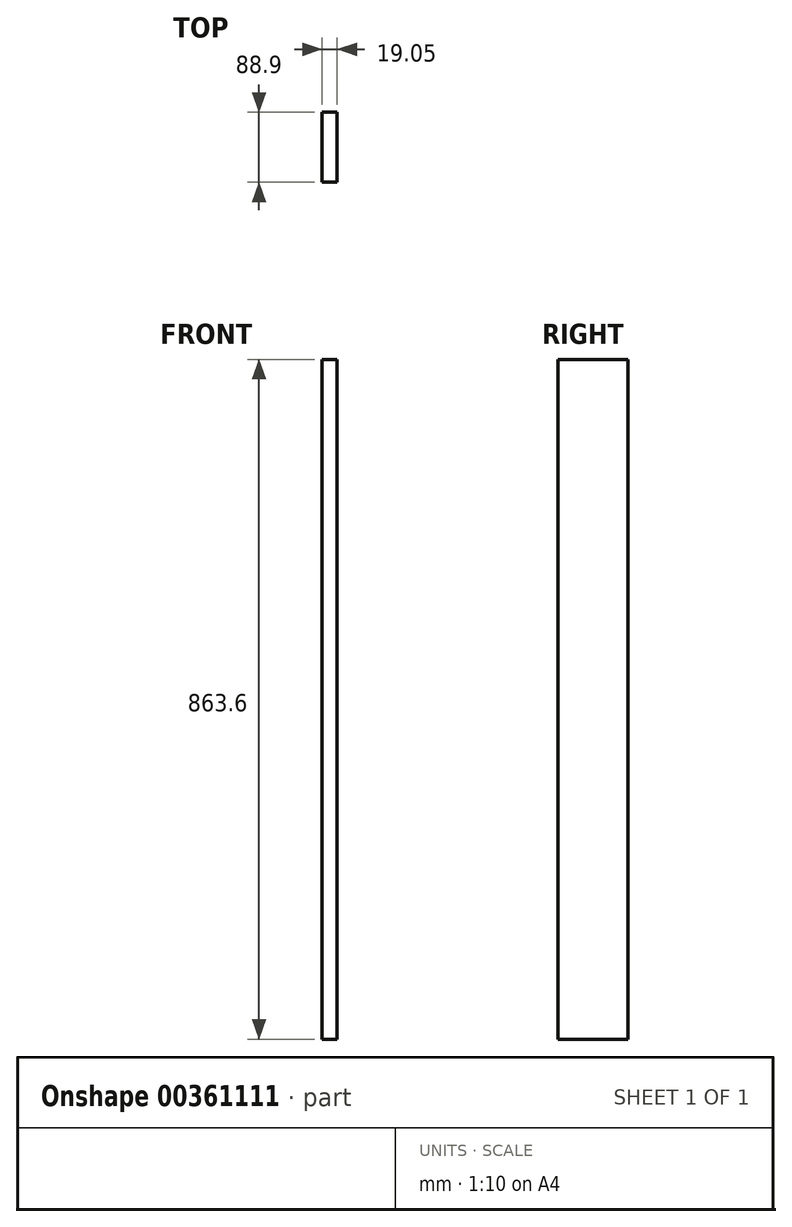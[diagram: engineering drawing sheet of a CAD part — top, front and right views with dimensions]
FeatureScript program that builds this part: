
annotation { "Feature Type Name" : "Feature", "Feature Type Description" : "" }
export const myFeature = defineFeature(function(context is Context, id is Id, definition is map)
    precondition{}
    {
        {
            var Q0;
            Q0=qCreatedBy(makeId("Front.planeOp"),FACE);
            var sketch = newSketch(context, id + "F0", { "sketchPlane" : qUnion([Q0])});
            skLineSegment(sketch, "E0.bottom", {"start": v(-7.55, 843.42) * mm, "end": v(11.5, 843.42) * mm});
            skLineSegment(sketch, "E0.top", {"start": v(-7.55, -20.18) * mm, "end": v(11.5, -20.18) * mm});
            skLineSegment(sketch, "E0.left", {"start": v(-7.55, 843.42) * mm, "end": v(-7.55, -20.18) * mm});
            skLineSegment(sketch, "E0.right", {"start": v(11.5, 843.42) * mm, "end": v(11.5, -20.18) * mm});
            skSolve(sketch);
        }
        {
            var Q0;
            Q0 = qSketchRegion(id + "F0", true);
            extrude(context, id + "F1", {"entities" : qUnion([Q0]), "depth" : 88.9 * mm});
        }
    });
